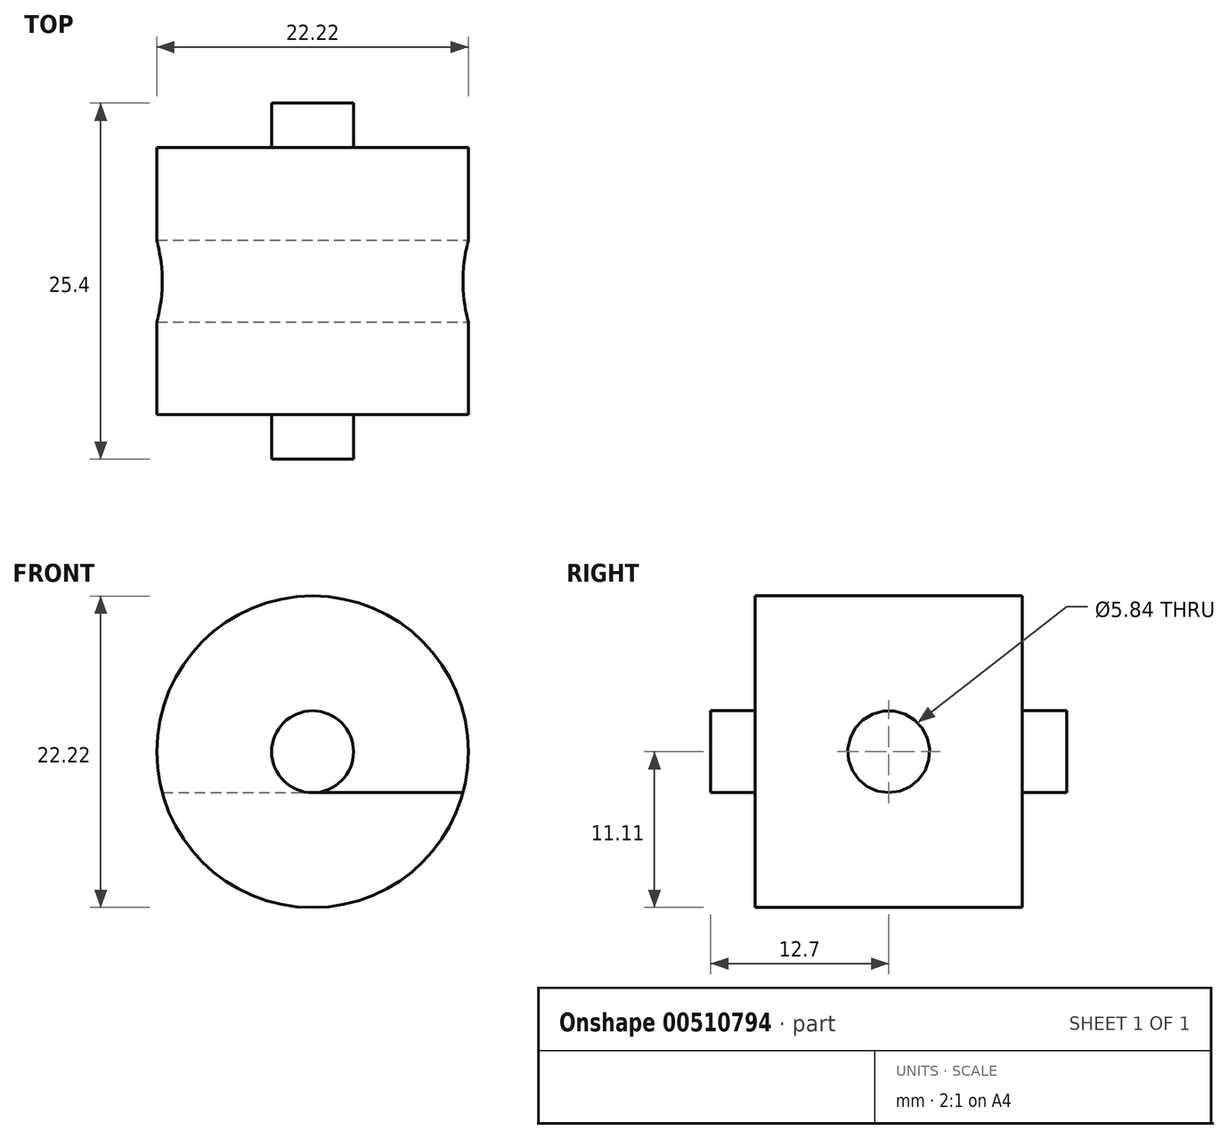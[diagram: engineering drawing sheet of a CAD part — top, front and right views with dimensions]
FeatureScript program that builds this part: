
annotation { "Feature Type Name" : "Feature", "Feature Type Description" : "" }
export const myFeature = defineFeature(function(context is Context, id is Id, definition is map)
    precondition{}
    {
        {
            var Q0;
            Q0=qCreatedBy(makeId("Front.planeOp"),FACE);
            var sketch = newSketch(context, id + "F0", { "sketchPlane" : qUnion([Q0])});
            skCircle(sketch, "E0", {"center": v(0, 0) * mm, "radius": 11.11 * mm});
            skCircle(sketch, "E1", {"center": v(0, 0) * mm, "radius": 2.92 * mm});
            skSolve(sketch);
        }
        {
            var Q0;
            Q0=makeQuery(id+"F0.imprint","IMPRINT",FACE,{"disambiguationData":[TD([[makeQuery(id+"F0.imprint","IMPRINT",EDGE,{"derivedFrom":sQuery(id+"F0.wireOp",EDGE,"E0")}),1.0]])]});
            var Q1;
            Q1=sQuery(id+"F0.wireOp",EDGE,"E0");
            extrude(context, id + "F1", {"entities" : qUnion([Q0]), "surfaceEntities" : qUnion([Q1]), "endBound" : BoundingType.SYMMETRIC, "depth" : 19.05 * mm, "offsetDistance" : 25.4 * mm, "hasSecondDirection" : true, "secondDirectionOppositeDirection" : true, "secondDirectionDepth" : 25.4 * mm});
        }
        {
            var Q0;
            Q0=makeQuery(id+"F0.imprint","IMPRINT",FACE,{"disambiguationData":[TD([[makeQuery(id+"F0.imprint","IMPRINT",EDGE,{"derivedFrom":sQuery(id+"F0.wireOp",EDGE,"E1")}),1.0]])]});
            extrude(context, id + "F2", {"entities" : qUnion([Q0]), "operationType" : NewBodyOperationType.ADD, "endBound" : BoundingType.SYMMETRIC, "depth" : 25.4 * mm, "offsetDistance" : 25.4 * mm});
        }
        {
            var Q0;
            Q0=qCreatedBy(makeId("Right.planeOp"),FACE);
            var sketch = newSketch(context, id + "F3", { "sketchPlane" : qUnion([Q0])});
            skCircle(sketch, "E2", {"center": v(0, 0) * mm, "radius": 2.92 * mm});
            skSolve(sketch);
        }
        {
            var Q0;
            Q0=makeQuery(id+"F3.imprint","IMPRINT",FACE,{"disambiguationData":[TD([[makeQuery(id+"F3.imprint","IMPRINT",EDGE,{"derivedFrom":sQuery(id+"F3.wireOp",EDGE,"E2")}),1.0]])]});
            var Q1;
            Q1=sQuery(id+"F3.wireOp",EDGE,"E2");
            extrude(context, id + "F4", {"entities" : qUnion([Q0]), "operationType" : NewBodyOperationType.REMOVE, "surfaceEntities" : qUnion([Q1]), "endBound" : BoundingType.SYMMETRIC, "oppositeDirection" : true, "depth" : 55.63 * mm, "offsetDistance" : 25.4 * mm});
        }
    });
